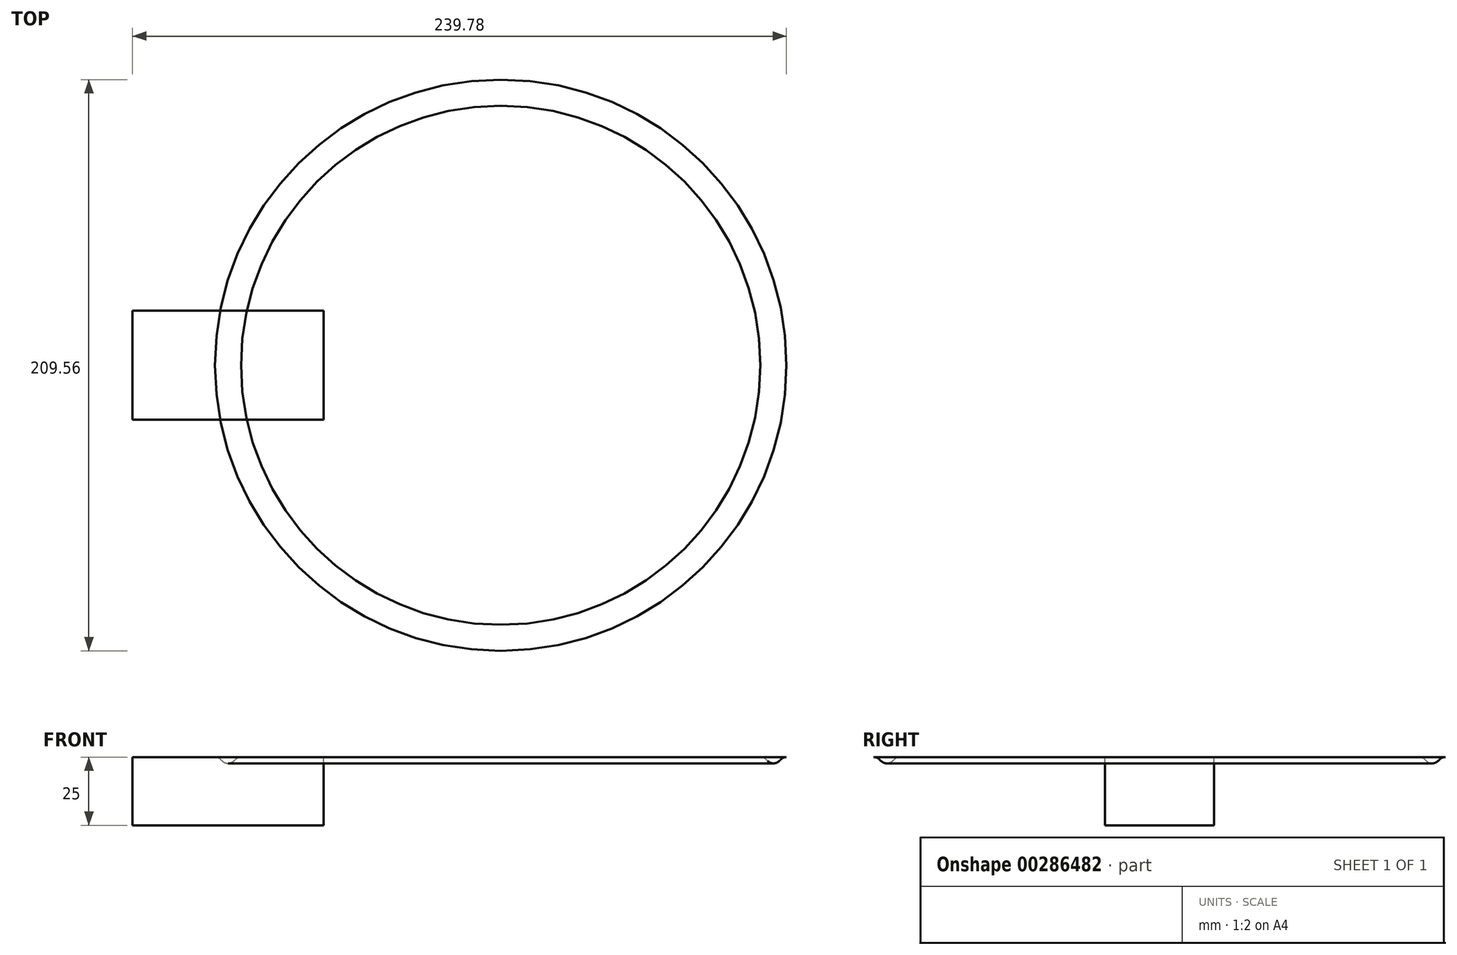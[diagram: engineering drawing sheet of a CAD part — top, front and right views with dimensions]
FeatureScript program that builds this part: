
annotation { "Feature Type Name" : "Feature", "Feature Type Description" : "" }
export const myFeature = defineFeature(function(context is Context, id is Id, definition is map)
    precondition{}
    {
        {
            var Q0;
            Q0=qCreatedBy(makeId("Top.planeOp"),FACE);
            var sketch = newSketch(context, id + "F0", { "sketchPlane" : qUnion([Q0])});
            skLineSegment(sketch, "E0.bottom", {"start": v(35, 20) * mm, "end": v(-35, 20) * mm});
            skLineSegment(sketch, "E0.top", {"start": v(35, -20) * mm, "end": v(-35, -20) * mm});
            skLineSegment(sketch, "E0.left", {"start": v(35, 20) * mm, "end": v(35, -20) * mm});
            skLineSegment(sketch, "E0.right", {"start": v(-35, 20) * mm, "end": v(-35, -20) * mm});
            skPoint(sketch, "E0.middle", {"position": v(0, 0) * mm});
            skSolve(sketch);
        }
        {
            var Q0;
            Q0 = qSketchRegion(id + "F0", true);
            extrude(context, id + "F1", {"entities" : qUnion([Q0]), "oppositeDirection" : true, "depth" : 25 * mm, "offsetDistance" : 25 * mm});
        }
        {
            var Q0;
            Q0=qCreatedBy(makeId("Front.planeOp"),FACE);
            var sketch = newSketch(context, id + "F2", { "sketchPlane" : qUnion([Q0])});
            skLineSegment(sketch, "E1", {"start": v(-40.92, 0) * mm, "end": v(0.08, 0) * mm});
            skLineSegment(sketch, "E2", {"start": v(-3.54, 0) * mm, "end": v(-2.12, -1.41) * mm});
            skLineSegment(sketch, "E3", {"start": v(2.12, -1.41) * mm, "end": v(2.66, -0.88) * mm});
            skPoint(sketch, "E4.visualSharp", {"position": v(3.54, 0) * mm});
            skArc(sketch, "E4.filletArc", {"start": v(4.78, 0) * mm, "mid": v(3.63, -0.23) * mm, "end": v(2.66, -0.88) * mm});
            skPoint(sketch, "E5.visualSharp", {"position": v(0, -3.54) * mm});
            skArc(sketch, "E5.filletArc", {"start": v(-2.12, -1.41) * mm, "mid": v(0, -2.3) * mm, "end": v(2.12, -1.41) * mm});
            skArc(sketch, "E6.MirrorCS", {"start": v(-4.78, 0) * mm, "mid": v(-3.63, -0.23) * mm, "end": v(-2.66, -0.88) * mm});
            skLineSegment(sketch, "E7", {"start": v(0, 0) * mm, "end": v(4.78, 0) * mm});
            skLineSegment(sketch, "E8", {"start": v(100, 0) * mm, "end": v(100, -28.53) * mm});
            skSolve(sketch);
        }
        {
            var Q0;
            Q0 = qSketchRegion(id + "F2", true);
            var Q1;
            Q1=sQuery(id+"F2.wireOp",EDGE,"E8");
            revolve(context, id + "F3", {"surfaceOperationType" : NewSurfaceOperationType.NEW, "entities" : qUnion([Q0]), "axis" : qUnion([Q1]), "revolveType" : RevolveType.FULL});
        }
    });
